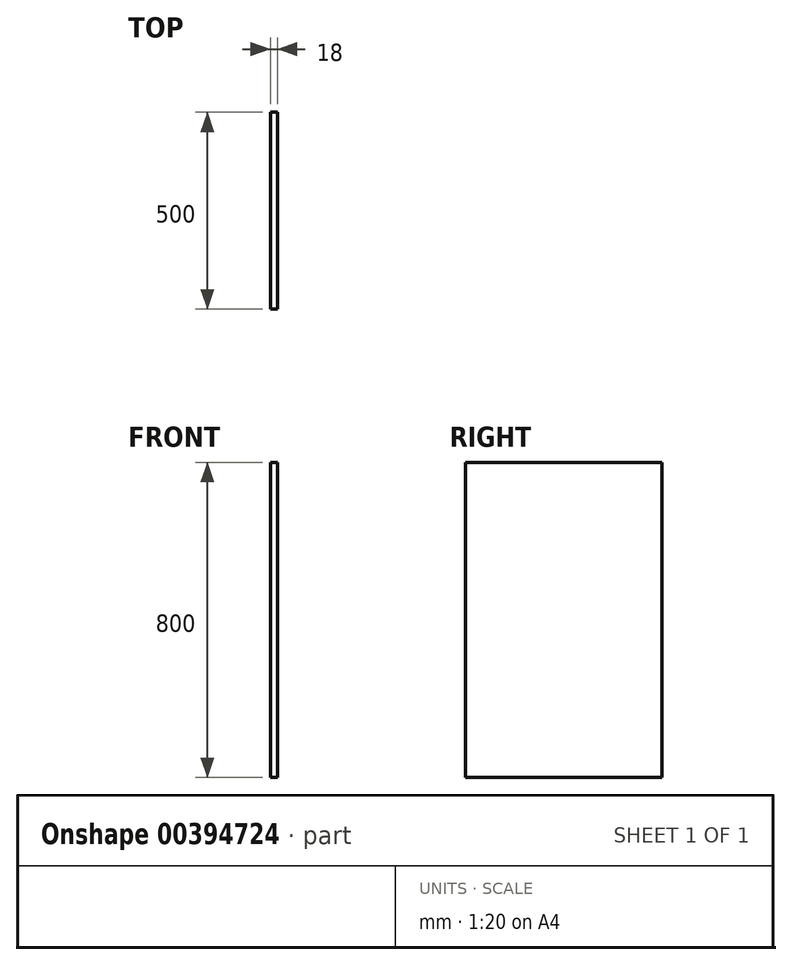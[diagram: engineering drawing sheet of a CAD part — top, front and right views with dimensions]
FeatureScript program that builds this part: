
annotation { "Feature Type Name" : "Feature", "Feature Type Description" : "" }
export const myFeature = defineFeature(function(context is Context, id is Id, definition is map)
    precondition{}
    {
        {
            var Q0;
            Q0=qCreatedBy(makeId("Right.planeOp"),FACE);
            var sketch = newSketch(context, id + "F0", { "sketchPlane" : qUnion([Q0])});
            skLineSegment(sketch, "E0.bottom", {"start": v(-404.25, 397.1) * mm, "end": v(95.75, 397.1) * mm});
            skLineSegment(sketch, "E0.top", {"start": v(-404.25, -402.9) * mm, "end": v(95.75, -402.9) * mm});
            skLineSegment(sketch, "E0.left", {"start": v(-404.25, 397.1) * mm, "end": v(-404.25, -402.9) * mm});
            skLineSegment(sketch, "E0.right", {"start": v(95.75, 397.1) * mm, "end": v(95.75, -402.9) * mm});
            skSolve(sketch);
        }
        {
            var Q0;
            Q0=makeQuery(id+"F0.imprint","IMPRINT",FACE,{"disambiguationData":[TD([[makeQuery(id+"F0.imprint","IMPRINT",EDGE,{"derivedFrom":sQuery(id+"F0.wireOp",EDGE,"E0.bottom")}),-1.0]])]});
            extrude(context, id + "F1", {"entities" : qUnion([Q0]), "depth" : 18 * mm});
        }
    });
